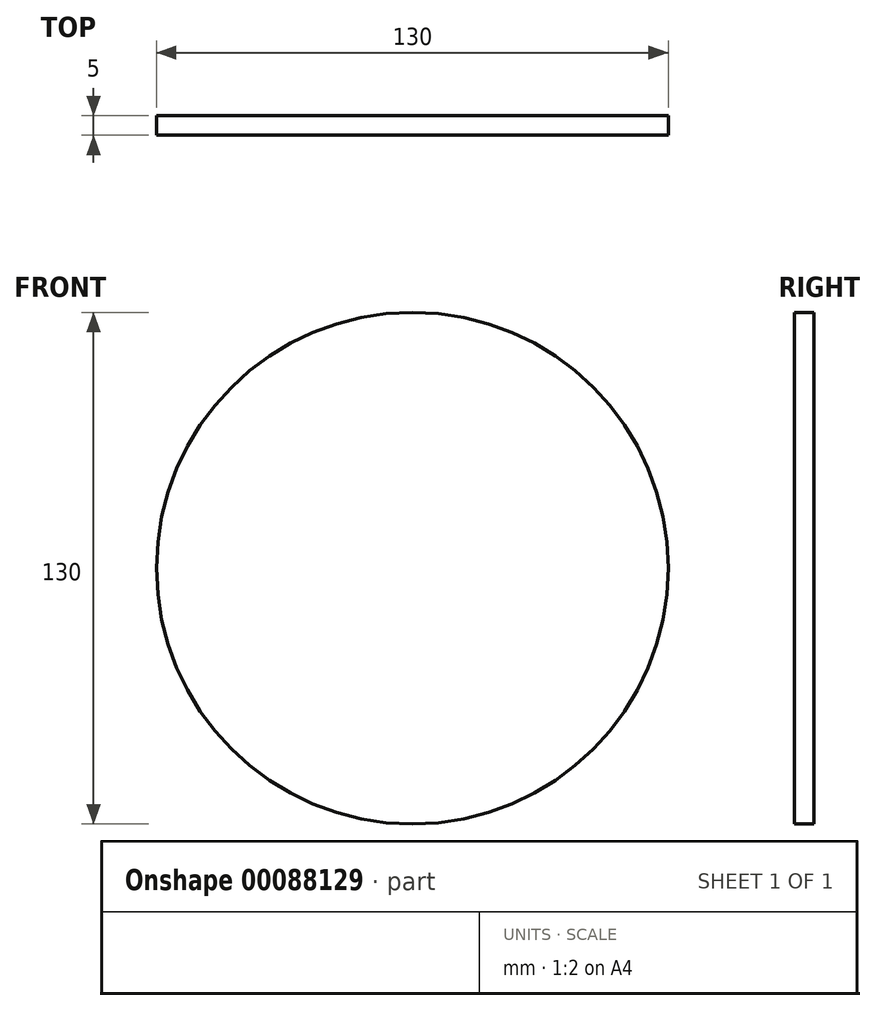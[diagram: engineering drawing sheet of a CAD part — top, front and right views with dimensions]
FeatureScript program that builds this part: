
annotation { "Feature Type Name" : "Feature", "Feature Type Description" : "" }
export const myFeature = defineFeature(function(context is Context, id is Id, definition is map)
    precondition{}
    {
        {
            var Q0;
            Q0=qCreatedBy(makeId("Front.planeOp"),FACE);
            var sketch = newSketch(context, id + "F0", { "sketchPlane" : qUnion([Q0])});
            skCircle(sketch, "E0", {"center": v(0, -2.04) * mm, "radius": 65 * mm});
            skSolve(sketch);
        }
        {
            var Q0;
            Q0=makeQuery(id+"F0.imprint","IMPRINT",FACE,{"disambiguationData":[TD([[makeQuery(id+"F0.imprint","IMPRINT",EDGE,{"derivedFrom":sQuery(id+"F0.wireOp",EDGE,"E0")}),1.0]])]});
            extrude(context, id + "F1", {"entities" : qUnion([Q0]), "depth" : 5 * mm});
        }
    });
